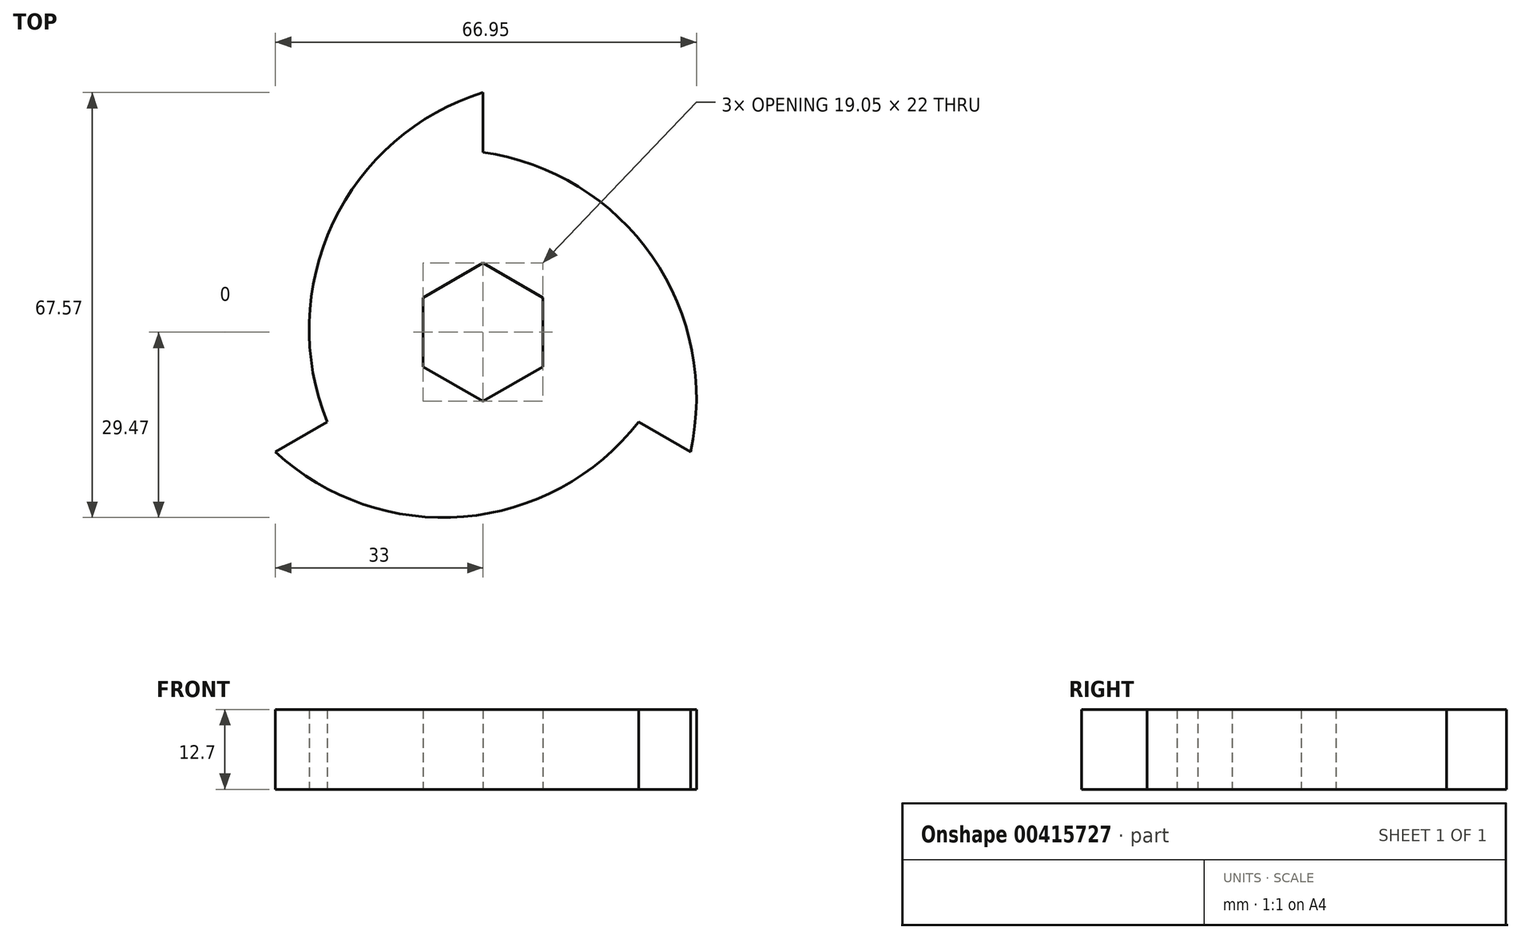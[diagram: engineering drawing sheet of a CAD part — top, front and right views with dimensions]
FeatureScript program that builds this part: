
annotation { "Feature Type Name" : "Feature", "Feature Type Description" : "" }
export const myFeature = defineFeature(function(context is Context, id is Id, definition is map)
    precondition{}
    {
        {
            var Q0;
            Q0=qCreatedBy(makeId("Top.planeOp"),FACE);
            var sketch = newSketch(context, id + "F0", { "sketchPlane" : qUnion([Q0])});
            skCircle(sketch, "E0", {"center": v(0, 0) * mm, "radius": 38.1 * mm, "construction": true});
            skLineSegment(sketch, "E1", {"start": v(0, 0) * mm, "end": v(0, 38.1) * mm, "construction": true});
            skLineSegment(sketch, "E2", {"start": v(0, 0) * mm, "end": v(33, -19.05) * mm, "construction": true});
            skLineSegment(sketch, "E3", {"start": v(0, 0) * mm, "end": v(-33, -19.05) * mm, "construction": true});
            skArc(sketch, "E4", {"start": v(0, 38.1) * mm, "mid": v(-23.87, 17.33) * mm, "end": v(-24.75, -14.29) * mm});
            skArc(sketch, "E5", {"start": v(-33, -19.05) * mm, "mid": v(-3.08, -29.34) * mm, "end": v(24.75, -14.29) * mm});
            skArc(sketch, "E6", {"start": v(33, -19.05) * mm, "mid": v(26.94, 12) * mm, "end": v(0, 28.58) * mm});
            skLineSegment(sketch, "E7", {"start": v(0, 38.1) * mm, "end": v(0, 28.58) * mm});
            skLineSegment(sketch, "E8", {"start": v(24.75, -14.29) * mm, "end": v(33, -19.05) * mm});
            skLineSegment(sketch, "E9", {"start": v(-33, -19.05) * mm, "end": v(-24.75, -14.29) * mm});
            skCircle(sketch, "E10.cCircle", {"center": v(0, 0) * mm, "radius": 9.53 * mm, "construction": true});
            skLineSegment(sketch, "E10.0", {"start": v(9.53, 5.5) * mm, "end": v(9.53, -5.5) * mm});
            skLineSegment(sketch, "E10.1", {"start": v(9.53, -5.5) * mm, "end": v(0, -11) * mm});
            skLineSegment(sketch, "E10.2", {"start": v(0, -11) * mm, "end": v(-9.53, -5.5) * mm});
            skLineSegment(sketch, "E10.3", {"start": v(-9.53, -5.5) * mm, "end": v(-9.53, 5.5) * mm});
            skLineSegment(sketch, "E10.4", {"start": v(-9.53, 5.5) * mm, "end": v(0, 11) * mm});
            skLineSegment(sketch, "E10.5", {"start": v(0, 11) * mm, "end": v(9.53, 5.5) * mm});
            skPoint(sketch, "E10.0.midPoint", {"position": v(9.53, 0) * mm});
            skLineSegment(sketch, "E11", {"start": v(0, 0) * mm, "end": v(19.8, 19.8) * mm, "construction": true});
            skLineSegment(sketch, "E12", {"start": v(19.8, 19.8) * mm, "end": v(26.94, 26.94) * mm, "construction": true});
            skSolve(sketch);
        }
        {
            var Q0;
            Q0 = qSketchRegion(id + "F0", true);
            extrude(context, id + "F1", {"entities" : qUnion([Q0]), "depth" : 12.7 * mm});
        }
    });
